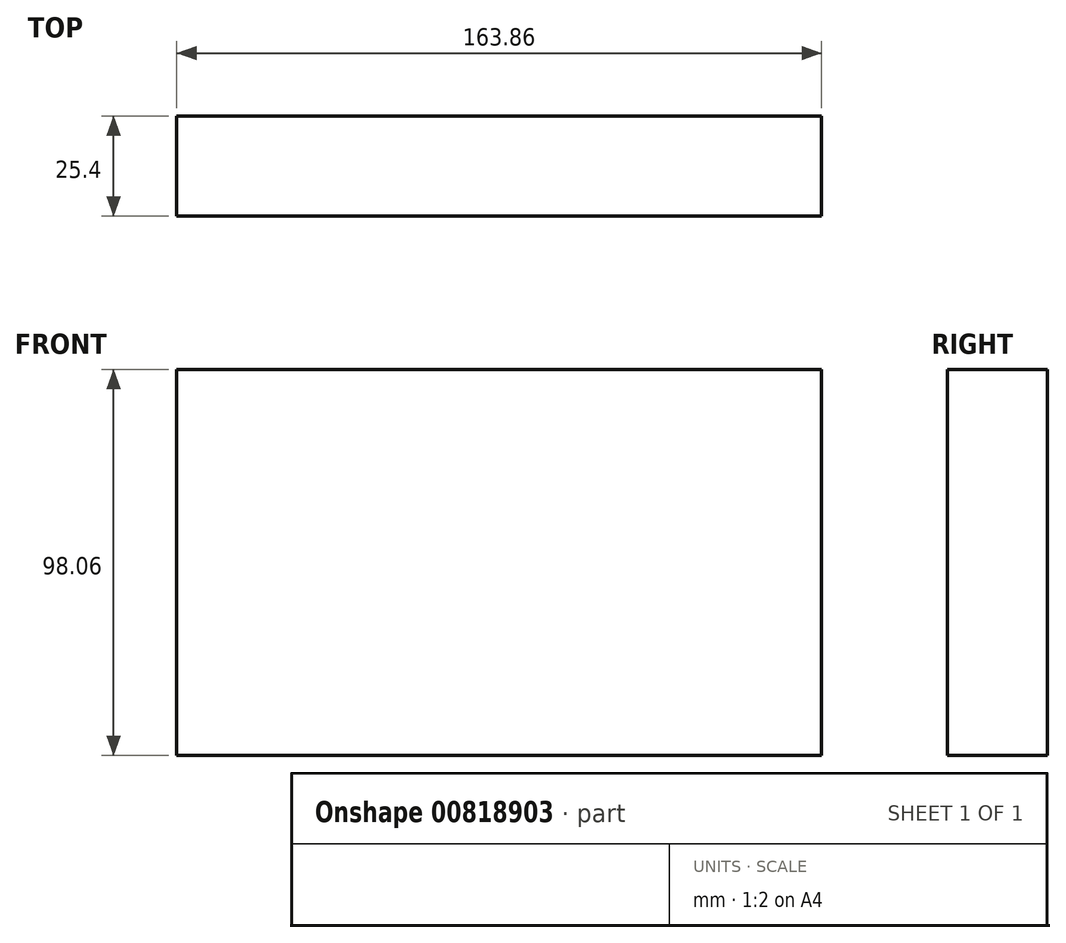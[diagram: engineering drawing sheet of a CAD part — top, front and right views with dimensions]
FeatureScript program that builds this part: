
annotation { "Feature Type Name" : "Feature", "Feature Type Description" : "" }
export const myFeature = defineFeature(function(context is Context, id is Id, definition is map)
    precondition{}
    {
        {
            var Q0;
            Q0=qCreatedBy(makeId("Front.planeOp"),FACE);
            var sketch = newSketch(context, id + "F0", { "sketchPlane" : qUnion([Q0])});
            skLineSegment(sketch, "E0", {"start": v(0, 0) * mm, "end": v(88.76, 0) * mm});
            skLineSegment(sketch, "E1", {"start": v(88.76, 0) * mm, "end": v(88.76, 98.06) * mm});
            skLineSegment(sketch, "E2", {"start": v(88.76, 98.06) * mm, "end": v(-75.1, 98.06) * mm});
            skLineSegment(sketch, "E3", {"start": v(-75.1, 98.06) * mm, "end": v(-75.1, 0) * mm});
            skLineSegment(sketch, "E4", {"start": v(-75.1, 0) * mm, "end": v(0, 0) * mm});
            skSolve(sketch);
        }
        {
            var Q0;
            Q0=makeQuery(id+"F0.imprint","IMPRINT",FACE,{"disambiguationData":[TD([[makeQuery(id+"F0.imprint","IMPRINT",EDGE,{"derivedFrom":sQuery(id+"F0.wireOp",EDGE,"E0")}),1.0]])]});
            extrude(context, id + "F1", {"entities" : qUnion([Q0]), "depth" : 25.4 * mm, "offsetDistance" : 25.4 * mm});
        }
    });
